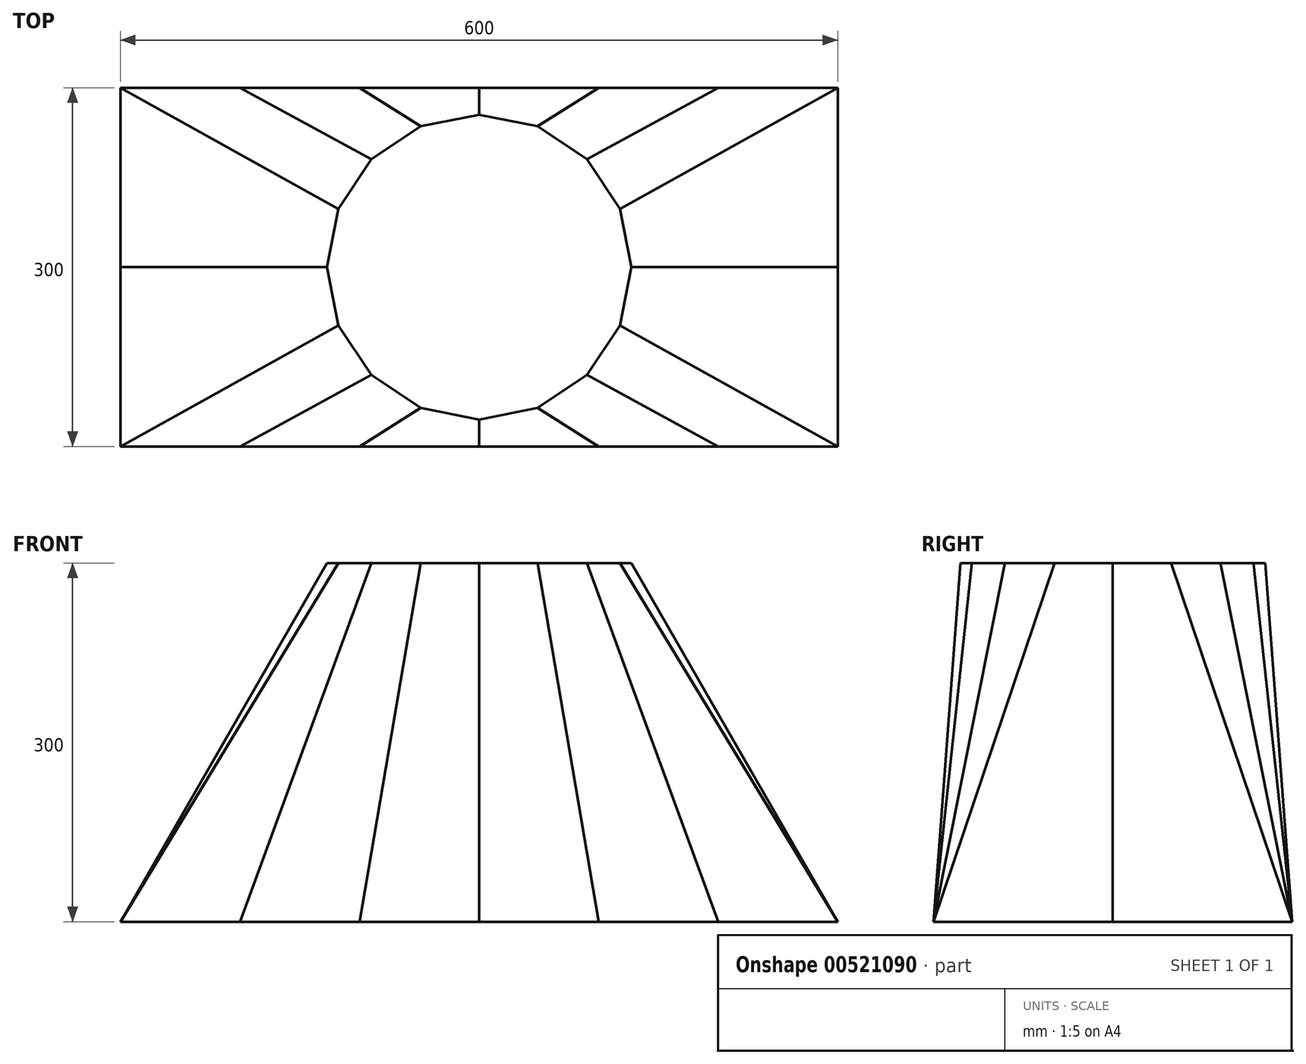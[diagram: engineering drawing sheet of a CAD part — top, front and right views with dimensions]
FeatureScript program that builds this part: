
annotation { "Feature Type Name" : "Feature", "Feature Type Description" : "" }
export const myFeature = defineFeature(function(context is Context, id is Id, definition is map)
    precondition{}
    {
        {
            var Q0;
            Q0=qCreatedBy(makeId("Top.planeOp"),FACE);
            var sketch = newSketch(context, id + "F0", { "sketchPlane" : qUnion([Q0])});
            skCircle(sketch, "E0.cCircle", {"center": v(0, 0) * mm, "radius": 125 * mm, "construction": true});
            skLineSegment(sketch, "E0.0", {"start": v(-90.12, -90.12) * mm, "end": v(-117.75, -48.77) * mm});
            skLineSegment(sketch, "E0.1", {"start": v(-117.75, -48.77) * mm, "end": v(-127.45, 0) * mm});
            skLineSegment(sketch, "E0.2", {"start": v(-127.45, 0) * mm, "end": v(-117.75, 48.77) * mm});
            skLineSegment(sketch, "E0.3", {"start": v(-117.75, 48.77) * mm, "end": v(-90.12, 90.12) * mm});
            skLineSegment(sketch, "E0.4", {"start": v(-90.12, 90.12) * mm, "end": v(-48.77, 117.75) * mm});
            skLineSegment(sketch, "E0.5", {"start": v(-48.77, 117.75) * mm, "end": v(0, 127.45) * mm});
            skLineSegment(sketch, "E0.6", {"start": v(0, 127.45) * mm, "end": v(48.77, 117.75) * mm});
            skLineSegment(sketch, "E0.7", {"start": v(48.77, 117.75) * mm, "end": v(90.12, 90.12) * mm});
            skLineSegment(sketch, "E0.8", {"start": v(90.12, 90.12) * mm, "end": v(117.75, 48.77) * mm});
            skLineSegment(sketch, "E0.9", {"start": v(117.75, 48.77) * mm, "end": v(127.45, 0) * mm});
            skLineSegment(sketch, "E0.10", {"start": v(127.45, 0) * mm, "end": v(117.75, -48.77) * mm});
            skLineSegment(sketch, "E0.11", {"start": v(117.75, -48.77) * mm, "end": v(90.12, -90.12) * mm});
            skLineSegment(sketch, "E0.12", {"start": v(90.12, -90.12) * mm, "end": v(48.77, -117.75) * mm});
            skLineSegment(sketch, "E0.13", {"start": v(48.77, -117.75) * mm, "end": v(0, -127.45) * mm});
            skLineSegment(sketch, "E0.14", {"start": v(0, -127.45) * mm, "end": v(-48.77, -117.75) * mm});
            skLineSegment(sketch, "E0.15", {"start": v(-48.77, -117.75) * mm, "end": v(-90.12, -90.12) * mm});
            skPoint(sketch, "E0.0.midPoint", {"position": v(-103.93, -69.45) * mm});
            skSolve(sketch);
        }
        {
            var Q0;
            Q0=qCreatedBy(makeId("Top.planeOp"),FACE);
            cPlane(context, id + "F1", {"entities" : qUnion([Q0]), "cplaneType" : CPlaneType.OFFSET, "offset" : 300 * mm, "oppositeDirection" : true, "width" : 150 * mm, "height" : 150 * mm});
        }
        {
            var Q0;
            Q0=qCreatedBy(id+"F1.planeOp",FACE);
            var sketch = newSketch(context, id + "F2", { "sketchPlane" : qUnion([Q0])});
            skLineSegment(sketch, "E1.bottom", {"start": v(-300, -150) * mm, "end": v(300, -150) * mm});
            skLineSegment(sketch, "E1.top", {"start": v(-300, 150) * mm, "end": v(300, 150) * mm});
            skLineSegment(sketch, "E1.left", {"start": v(-300, -150) * mm, "end": v(-300, 150) * mm});
            skLineSegment(sketch, "E1.right", {"start": v(300, -150) * mm, "end": v(300, 150) * mm});
            skPoint(sketch, "E1.middle", {"position": v(0, 0) * mm});
            skSolve(sketch);
        }
        {
            var Q0;
            Q0=qCreatedBy(makeId("Front.planeOp"),FACE);
            var sketch = newSketch(context, id + "F3", { "sketchPlane" : qUnion([Q0])});
            skLineSegment(sketch, "E2", {"start": v(-127.45, 0) * mm, "end": v(-300, -300) * mm});
            skLineSegment(sketch, "E3", {"start": v(127.45, 0) * mm, "end": v(300, -300) * mm});
            skSolve(sketch);
        }
        {
            var Q0;
            Q0=qCreatedBy(makeId("Right.planeOp"),FACE);
            var sketch = newSketch(context, id + "F4", { "sketchPlane" : qUnion([Q0])});
            skLineSegment(sketch, "E4", {"start": v(127.45, 0) * mm, "end": v(150, -300) * mm});
            skLineSegment(sketch, "E5", {"start": v(-127.45, 0) * mm, "end": v(-150, -300) * mm});
            skSolve(sketch);
        }
        {
            var Q0;
            Q0=sQuery(id+"F2.wireOp",VERTEX,"E1.left.end");
            var Q1;
            Q1=sQuery(id+"F0.wireOp",VERTEX,"E0.3.start");
            var Q2;
            Q2=sQuery(id+"F2.wireOp",VERTEX,"E1.right.start");
            cPlane(context, id + "F5", {"entities" : qUnion([Q0, Q1, Q2]), "cplaneType" : CPlaneType.THREE_POINT, "offset" : 25 * mm, "width" : 150 * mm, "height" : 150 * mm});
        }
        {
            var Q0;
            Q0=sQuery(id+"F2.wireOp",VERTEX,"E1.bottom.start");
            var Q1;
            Q1=sQuery(id+"F0.wireOp",VERTEX,"E0.1.start");
            var Q2;
            Q2=sQuery(id+"F2.wireOp",VERTEX,"E1.right.end");
            cPlane(context, id + "F6", {"entities" : qUnion([Q0, Q1, Q2]), "cplaneType" : CPlaneType.THREE_POINT, "offset" : 25 * mm, "width" : 150 * mm, "height" : 150 * mm});
        }
        {
            var Q0;
            Q0=qCreatedBy(id+"F5.planeOp",FACE);
            var sketch = newSketch(context, id + "F7", { "sketchPlane" : qUnion([Q0])});
            skLineSegment(sketch, "E6", {"start": v(-127.12, -1.64) * mm, "end": v(-330.86, -304.88) * mm});
            skSolve(sketch);
        }
        {
            var Q0;
            Q0=qCreatedBy(id+"F6.planeOp",FACE);
            var sketch = newSketch(context, id + "F8", { "sketchPlane" : qUnion([Q0])});
            skLineSegment(sketch, "E7", {"start": v(-127.12, -1.64) * mm, "end": v(-330.86, -304.88) * mm});
            skSolve(sketch);
        }
        {
            var Q0;
            Q0=sQuery(id+"F0.wireOp",VERTEX,"E0.11.start");
            var Q1;
            Q1=sQuery(id+"F2.wireOp",VERTEX,"E1.right.start");
            var Q2;
            Q2=sQuery(id+"F2.wireOp",VERTEX,"E1.top.start");
            cPlane(context, id + "F9", {"entities" : qUnion([Q0, Q1, Q2]), "cplaneType" : CPlaneType.THREE_POINT, "offset" : 25 * mm, "width" : 150 * mm, "height" : 150 * mm});
        }
        {
            var Q0;
            Q0=qCreatedBy(id+"F9.planeOp",FACE);
            var sketch = newSketch(context, id + "F10", { "sketchPlane" : qUnion([Q0])});
            skLineSegment(sketch, "E8", {"start": v(127.12, -1.64) * mm, "end": v(330.86, -304.88) * mm});
            skSolve(sketch);
        }
        {
            var Q0;
            Q0=sQuery(id+"F2.wireOp",VERTEX,"E1.right.end");
            var Q1;
            Q1=sQuery(id+"F0.wireOp",VERTEX,"E0.9.start");
            var Q2;
            Q2=sQuery(id+"F8.wireOp",VERTEX,"E7.end");
            cPlane(context, id + "F11", {"entities" : qUnion([Q0, Q1, Q2]), "cplaneType" : CPlaneType.THREE_POINT, "offset" : 25 * mm, "width" : 150 * mm, "height" : 150 * mm});
        }
        {
            var Q0;
            Q0=qCreatedBy(id+"F11.planeOp",FACE);
            var sketch = newSketch(context, id + "F12", { "sketchPlane" : qUnion([Q0])});
            skLineSegment(sketch, "E9", {"start": v(-127.12, -1.64) * mm, "end": v(-330.86, -304.88) * mm});
            skSolve(sketch);
        }
        {
            var Q0;
            Q0 = qSketchRegion(id + "F0", true);
            var Q1;
            Q1 = qSketchRegion(id + "F2", true);
            var Q2;
            Q2=sQuery(id+"F3.wireOp",EDGE,"E3");
            var Q3;
            Q3=sQuery(id+"F3.wireOp",EDGE,"E2");
            var Q4;
            Q4=sQuery(id+"F12.wireOp",EDGE,"E9");
            var Q5;
            Q5=sQuery(id+"F10.wireOp",EDGE,"E8");
            var Q6;
            Q6=sQuery(id+"F4.wireOp",EDGE,"E4");
            var Q7;
            Q7=sQuery(id+"F4.wireOp",EDGE,"E5");
            var Q8;
            Q8=sQuery(id+"F8.wireOp",EDGE,"E7");
            var Q9;
            Q9=sQuery(id+"F7.wireOp",EDGE,"E6");
            var Q10;
            Q10=sQuery(id+"F3.wireOp",VERTEX,"E2.start");
            var Q11;
            Q11=sQuery(id+"F3.wireOp",VERTEX,"E2.end");
            loft(context, id + "F13", {"addGuides" : true, "sheetProfilesArray" : [{ "sheetProfileEntities" : qUnion([Q0]) }, { "sheetProfileEntities" : qUnion([Q1]) }], "guidesArray" : [{ "guideEntities" : qUnion([Q2]), "guideDerivativeType" : LoftGuideDerivativeType.DEFAULT, "guideDerivativeMagnitude" : 1 }, { "guideEntities" : qUnion([Q3]), "guideDerivativeType" : LoftGuideDerivativeType.DEFAULT, "guideDerivativeMagnitude" : 1 }, { "guideEntities" : qUnion([Q4]), "guideDerivativeType" : LoftGuideDerivativeType.DEFAULT, "guideDerivativeMagnitude" : 1 }, { "guideEntities" : qUnion([Q5]), "guideDerivativeType" : LoftGuideDerivativeType.DEFAULT, "guideDerivativeMagnitude" : 1 }, { "guideEntities" : qUnion([Q6]), "guideDerivativeType" : LoftGuideDerivativeType.DEFAULT, "guideDerivativeMagnitude" : 1 }, { "guideEntities" : qUnion([Q7]), "guideDerivativeType" : LoftGuideDerivativeType.DEFAULT, "guideDerivativeMagnitude" : 1 }, { "guideEntities" : qUnion([Q8]), "guideDerivativeType" : LoftGuideDerivativeType.DEFAULT, "guideDerivativeMagnitude" : 1 }, { "guideEntities" : qUnion([Q9]), "guideDerivativeType" : LoftGuideDerivativeType.DEFAULT, "guideDerivativeMagnitude" : 1 }], "matchConnections" : true, "connections" : [{ "connectionEntities" : qUnion([Q10, Q11]), "connectionEdgeQueries" : qUnion([]), "connectionEdgeParameters" : [] }]});
        }
    });
